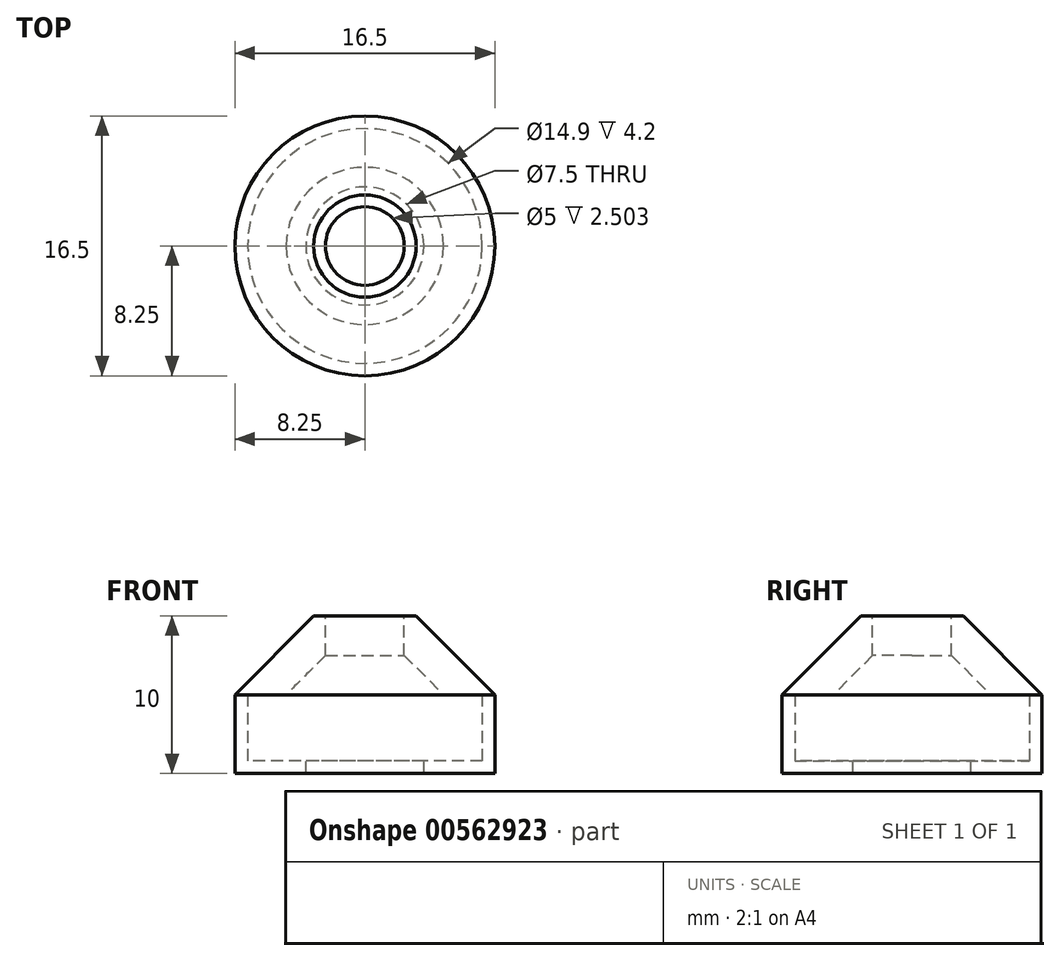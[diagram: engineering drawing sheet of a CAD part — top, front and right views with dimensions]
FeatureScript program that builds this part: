
annotation { "Feature Type Name" : "Feature", "Feature Type Description" : "" }
export const myFeature = defineFeature(function(context is Context, id is Id, definition is map)
    precondition{}
    {
        {
            var Q0;
            Q0=qCreatedBy(makeId("Top.planeOp"),FACE);
            var sketch = newSketch(context, id + "F0", { "sketchPlane" : qUnion([Q0])});
            skCircle(sketch, "E0", {"center": v(0, 0) * mm, "radius": 8.25 * mm});
            skSolve(sketch);
        }
        {
            var Q0;
            Q0 = qSketchRegion(id + "F0", true);
            extrude(context, id + "F1", {"entities" : qUnion([Q0]), "depth" : 5 * mm, "offsetDistance" : 25 * mm});
        }
        {
            var Q0;
            Q0=makeQuery(id+"F1.opExtrude","CAP_FACE",FACE,{"disambiguationData":[OSD([sQuery(id+"F0.wireOp",EDGE,"E0")])],"isStart":false});
            shell(context, id + "F2", {"entities" : qUnion([Q0]), "thickness" : 0.8 * mm});
        }
        {
            var Q0;
            {var subQ0=sQuery(id+"F0.wireOp",EDGE,"E0");Q0=makeQuery(id+"F2.opShell","OFFSET_FACE",FACE,{"disambiguationData":[OSD([subQ0]),TDD([makeQuery(id+"F1.opExtrude","CAP_FACE",FACE,{"disambiguationData":[OSD([subQ0])],"isStart":true})])]});}
            var sketch = newSketch(context, id + "F3", { "sketchPlane" : qUnion([Q0])});
            skCircle(sketch, "E1", {"center": v(0, 0) * mm, "radius": 3.75 * mm});
            skSolve(sketch);
        }
        {
            var Q0;
            Q0 = qSketchRegion(id + "F3", true);
            extrude(context, id + "F4", {"entities" : qUnion([Q0]), "operationType" : NewBodyOperationType.REMOVE, "oppositeDirection" : true, "depth" : 25 * mm, "offsetDistance" : 25 * mm});
        }
        {
            var Q0;
            Q0=makeQuery(id+"F1.opExtrude","CAP_FACE",FACE,{"disambiguationData":[OSD([sQuery(id+"F0.wireOp",EDGE,"E0")])],"isStart":false});
            var sketch = newSketch(context, id + "F5", { "sketchPlane" : qUnion([Q0])});
            skCircle(sketch, "E2", {"center": v(0, 0) * mm, "radius": 8.25 * mm});
            skSolve(sketch);
        }
        {
            var Q0;
            Q0 = qSketchRegion(id + "F5", true);
            extrude(context, id + "F6", {"entities" : qUnion([Q0]), "operationType" : NewBodyOperationType.ADD, "depth" : 5 * mm, "offsetDistance" : 25 * mm});
        }
        {
            var Q0;
            Q0=makeQuery(id+"F6.opExtrude","CAP_EDGE",EDGE,{"disambiguationData":[OSD([sQuery(id+"F5.wireOp",EDGE,"E2")])],"isStart":false});
            chamfer(context, id + "F7", {"entities" : qUnion([Q0]), "width" : 5 * mm, "tangentPropagation" : true});
        }
        {
            var Q0;
            Q0=makeQuery(id+"F6.opExtrude","CAP_FACE",FACE,{"disambiguationData":[OSD([sQuery(id+"F5.wireOp",EDGE,"E2")])],"isStart":true});
            shell(context, id + "F8", {"entities" : qUnion([Q0]), "thickness" : 2.3 * mm});
        }
        {
            var Q0;
            Q0=makeQuery(id+"F6.opExtrude","CAP_FACE",FACE,{"disambiguationData":[OSD([sQuery(id+"F5.wireOp",EDGE,"E2")])],"isStart":false});
            var sketch = newSketch(context, id + "F9", { "sketchPlane" : qUnion([Q0])});
            skCircle(sketch, "E3", {"center": v(0, 0) * mm, "radius": 2.5 * mm});
            skSolve(sketch);
        }
        {
            var Q0;
            Q0 = qSketchRegion(id + "F9", true);
            extrude(context, id + "F10", {"entities" : qUnion([Q0]), "operationType" : NewBodyOperationType.REMOVE, "oppositeDirection" : true, "depth" : 25 * mm, "offsetDistance" : 25 * mm});
        }
    });
